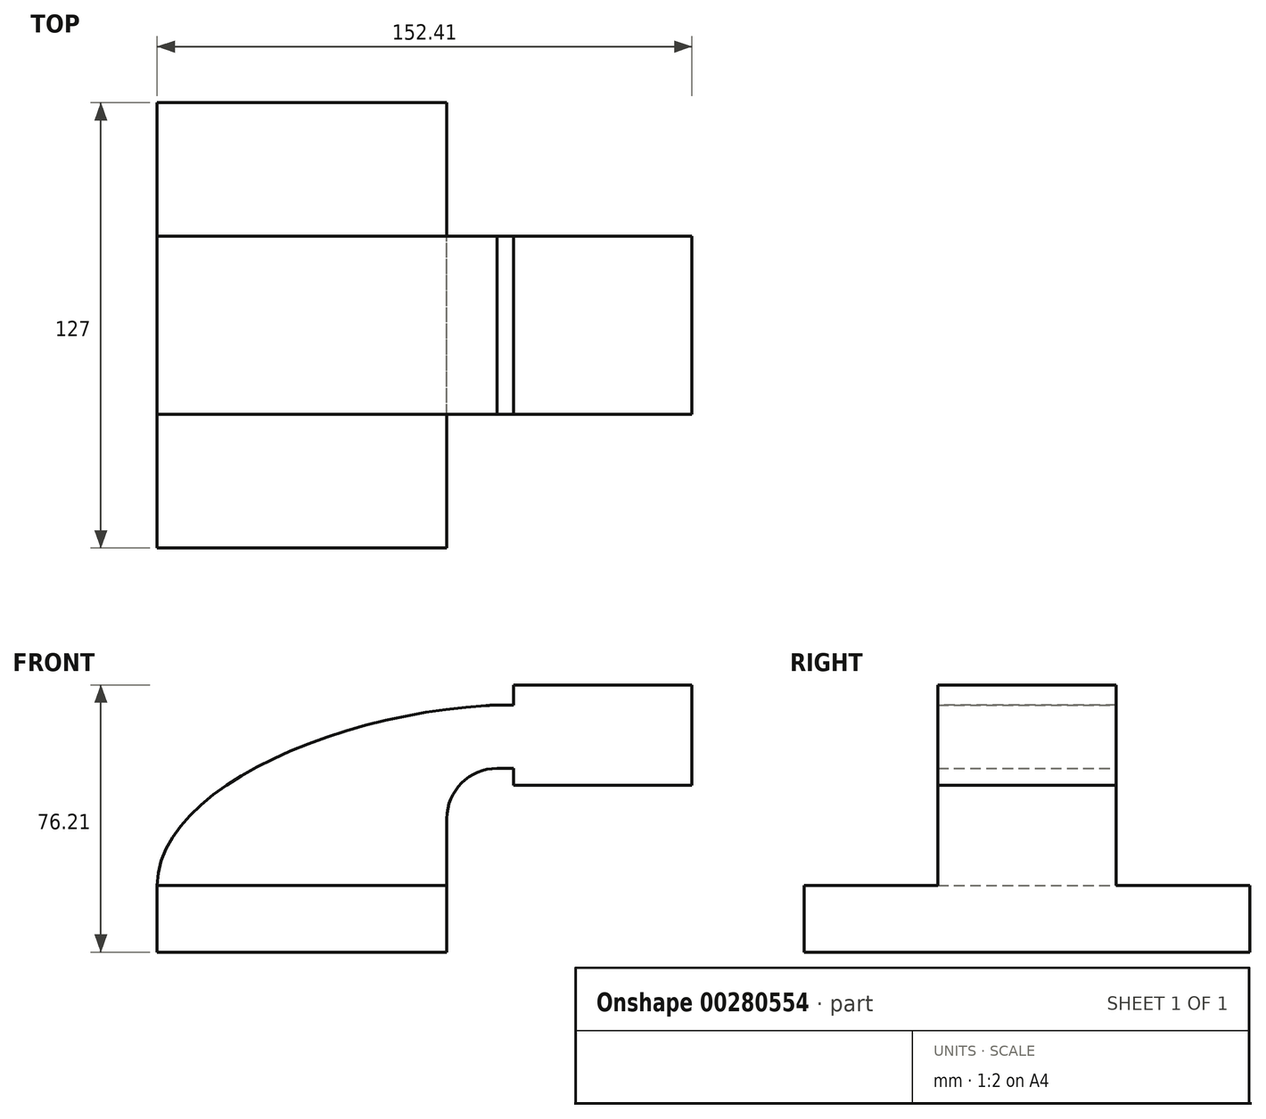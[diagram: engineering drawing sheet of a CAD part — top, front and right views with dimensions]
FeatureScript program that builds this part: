
annotation { "Feature Type Name" : "Feature", "Feature Type Description" : "" }
export const myFeature = defineFeature(function(context is Context, id is Id, definition is map)
    precondition{}
    {
        {
            var Q0;
            Q0=qCreatedBy(makeId("Front.planeOp"),FACE);
            var sketch = newSketch(context, id + "F0", { "sketchPlane" : qUnion([Q0])});
            skLineSegment(sketch, "E0.bottom", {"start": v(41.28, 9.53) * mm, "end": v(-41.28, 9.52) * mm});
            skLineSegment(sketch, "E0.top", {"start": v(41.28, -9.52) * mm, "end": v(-41.28, -9.53) * mm});
            skLineSegment(sketch, "E0.left", {"start": v(41.28, 9.53) * mm, "end": v(41.28, -9.52) * mm});
            skLineSegment(sketch, "E0.right", {"start": v(-41.28, 9.52) * mm, "end": v(-41.28, -9.53) * mm});
            skPoint(sketch, "E0.middle", {"position": v(0, 0) * mm});
            skLineSegment(sketch, "E1.bottom", {"start": v(60.33, 66.68) * mm, "end": v(111.13, 66.68) * mm});
            skLineSegment(sketch, "E1.top", {"start": v(60.33, 38.1) * mm, "end": v(111.13, 38.1) * mm});
            skLineSegment(sketch, "E1.left", {"start": v(60.33, 66.68) * mm, "end": v(60.33, 38.1) * mm});
            skLineSegment(sketch, "E1.right", {"start": v(111.13, 66.68) * mm, "end": v(111.13, 38.1) * mm});
            skPoint(sketch, "E1.middle", {"position": v(85.73, 52.39) * mm});
            skLineSegment(sketch, "E2", {"start": v(41.28, 9.53) * mm, "end": v(41.28, 28.54) * mm});
            skArc(sketch, "E3", {"start": v(41.28, 28.54) * mm, "mid": v(45.47, 38.68) * mm, "end": v(55.61, 42.88) * mm});
            skLineSegment(sketch, "E4", {"start": v(55.61, 42.88) * mm, "end": v(85.73, 42.88) * mm});
            skLineSegment(sketch, "E5.0", {"start": v(55.61, 60.93) * mm, "end": v(85.73, 60.93) * mm});
            skArc(sketch, "E5.1", {"start": v(23.22, 28.54) * mm, "mid": v(32.7, 51.45) * mm, "end": v(55.61, 60.93) * mm});
            skLineSegment(sketch, "E5.2", {"start": v(23.22, 9.53) * mm, "end": v(23.22, 28.54) * mm});
            skLineSegment(sketch, "E6", {"start": v(85.73, 66.68) * mm, "end": v(85.73, 38.1) * mm});
            skFitSpline(sketch, "E7", {"points": [v(-41.28, 9.52) * mm, v(55.61, 60.93) * mm], "startDerivative": vector(0.89, 84.04) * mm, "endDerivative": vector(132.03, 5.12) * mm});
            skSolve(sketch);
        }
        {
            var Q0;
            Q0=makeQuery(id+"F0.imprint","IMPRINT",FACE,{"disambiguationData":[TD([[makeQuery(id+"F0.imprint","IMPRINT",EDGE,{"derivedFrom":sQuery(id+"F0.wireOp",EDGE,"E0.top")}),-1.0]])]});
            extrude(context, id + "F1", {"entities" : qUnion([Q0]), "endBound" : BoundingType.SYMMETRIC, "depth" : 127 * mm});
        }
        {
            var Q0;
            {var subQ0=sQuery(id+"F0.wireOp",EDGE,"E7");var subQ1=sQuery(id+"F0.wireOp",EDGE,"E5.1");var subQ3=makeQuery(id+"F0.imprint","INTERSECT",VERTEX,{"derivedFrom":[subQ1,subQ0]});Q0=makeQuery(id+"F0.imprint","IMPRINT",FACE,{"disambiguationData":[TD([[makeQuery(id+"F0.imprint","IMPRINT",EDGE,{"disambiguationData":[TD([[subQ3,-1.0]])],"derivedFrom":subQ1}),-1.0]])]});}
            var Q1;
            Q1=makeQuery(id+"F0.imprint","IMPRINT",FACE,{"disambiguationData":[TD([[makeQuery(id+"F0.imprint","IMPRINT",EDGE,{"derivedFrom":sQuery(id+"F0.wireOp",EDGE,"E0.top")}),-1.0]])]});
            var Q2;
            {var subQ0=sQuery(id+"F0.wireOp",EDGE,"E1.left");var subQ1=sQuery(id+"F0.wireOp",EDGE,"E1.bottom");var subQ2=makeQuery(id+"F0.imprint","INTERSECT",VERTEX,{"derivedFrom":[subQ1,subQ0]});Q2=makeQuery(id+"F0.imprint","IMPRINT",FACE,{"disambiguationData":[TD([[makeQuery(id+"F0.imprint","IMPRINT",EDGE,{"disambiguationData":[TD([[subQ2,-1.0]])],"derivedFrom":subQ1}),-1.0]])]});}
            var Q3;
            {var subQ0=sQuery(id+"F0.wireOp",EDGE,"E1.left");var subQ1=sQuery(id+"F0.wireOp",EDGE,"E1.top");var subQ2=makeQuery(id+"F0.imprint","INTERSECT",VERTEX,{"derivedFrom":[subQ1,subQ0]});Q3=makeQuery(id+"F0.imprint","IMPRINT",FACE,{"disambiguationData":[TD([[makeQuery(id+"F0.imprint","IMPRINT",EDGE,{"disambiguationData":[TD([[subQ2,-1.0]])],"derivedFrom":subQ1}),1.0]])]});}
            var Q4;
            {var subQ4=sQuery(id+"F0.wireOp",EDGE,"E1.right");Q4=makeQuery(id+"F0.imprint","IMPRINT",FACE,{"disambiguationData":[TD([[makeQuery(id+"F0.imprint","IMPRINT",EDGE,{"derivedFrom":subQ4}),-1.0]])]});}
            var Q5;
            {var subQ0=sQuery(id+"F0.wireOp",EDGE,"E5.0");var subQ1=sQuery(id+"F0.wireOp",EDGE,"E1.left");var subQ2=makeQuery(id+"F0.imprint","INTERSECT",VERTEX,{"derivedFrom":[subQ1,subQ0]});Q5=makeQuery(id+"F0.imprint","IMPRINT",FACE,{"disambiguationData":[TD([[makeQuery(id+"F0.imprint","IMPRINT",EDGE,{"disambiguationData":[TD([[subQ2,-1.0]])],"derivedFrom":subQ1}),1.0]])]});}
            var Q6;
            {var subQ1=sQuery(id+"F0.wireOp",EDGE,"E2");Q6=makeQuery(id+"F0.imprint","IMPRINT",FACE,{"disambiguationData":[TD([[makeQuery(id+"F0.imprint","IMPRINT",EDGE,{"derivedFrom":subQ1}),1.0]])]});}
            extrude(context, id + "F2", {"entities" : qUnion([Q0, Q1, Q2, Q3, Q4, Q5, Q6]), "operationType" : NewBodyOperationType.ADD, "endBound" : BoundingType.SYMMETRIC, "depth" : 50.8 * mm});
        }
    });
